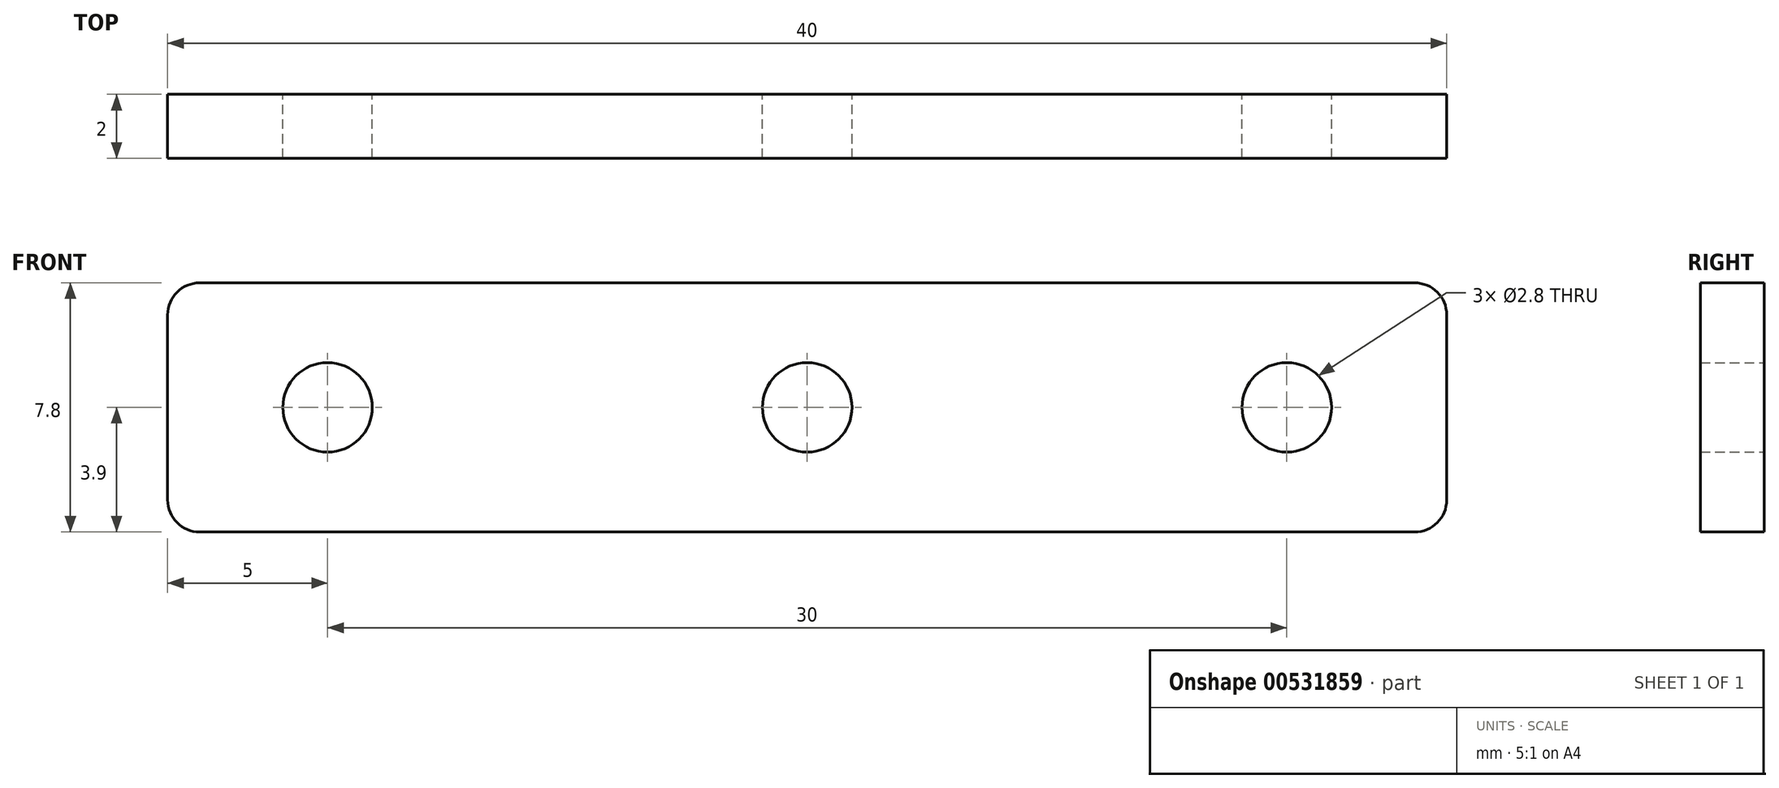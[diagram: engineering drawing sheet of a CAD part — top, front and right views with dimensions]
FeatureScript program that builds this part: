
annotation { "Feature Type Name" : "Feature", "Feature Type Description" : "" }
export const myFeature = defineFeature(function(context is Context, id is Id, definition is map)
    precondition{}
    {
        {
            var Q0;
            Q0=qCreatedBy(makeId("Front.planeOp"),FACE);
            var sketch = newSketch(context, id + "F0", { "sketchPlane" : qUnion([Q0])});
            skLineSegment(sketch, "E0.bottom", {"start": v(0, 0) * mm, "end": v(40, 0) * mm});
            skLineSegment(sketch, "E0.top", {"start": v(0, 7.8) * mm, "end": v(40, 7.8) * mm});
            skLineSegment(sketch, "E0.left", {"start": v(0, 0) * mm, "end": v(0, 7.8) * mm});
            skLineSegment(sketch, "E0.right", {"start": v(40, 0) * mm, "end": v(40, 7.8) * mm});
            skLineSegment(sketch, "E1", {"start": v(0, 3.9) * mm, "end": v(10, 3.9) * mm});
            skCircle(sketch, "E2", {"center": v(5, 3.9) * mm, "radius": 1.4 * mm});
            skLineSegment(sketch, "E3", {"start": v(40, 3.9) * mm, "end": v(30, 3.9) * mm});
            skPoint(sketch, "E3.endSnap0", {"position": v(40, 3.9) * mm});
            skCircle(sketch, "E4", {"center": v(35, 3.9) * mm, "radius": 1.4 * mm});
            skLineSegment(sketch, "E5", {"start": v(20, 7.8) * mm, "end": v(20, 3.9) * mm});
            skCircle(sketch, "E6", {"center": v(20, 3.9) * mm, "radius": 1.4 * mm});
            skSolve(sketch);
        }
        {
            var Q0;
            Q0=qSketchRegion(id+"F0",true);
            extrude(context, id + "F1", {"entities" : qUnion([Q0]), "depth" : 2 * mm});
        }
        {
            var Q0;
            Q0=makeQuery(id+"F1.opExtrude","SWEPT_EDGE",EDGE,{"disambiguationData":[OSD([sQuery(id+"F0.wireOp",EDGE,"E0.top"),sQuery(id+"F0.wireOp",EDGE,"E0.left")])]});
            var Q1;
            Q1=makeQuery(id+"F1.opExtrude","SWEPT_EDGE",EDGE,{"disambiguationData":[OSD([sQuery(id+"F0.wireOp",EDGE,"E0.bottom"),sQuery(id+"F0.wireOp",EDGE,"E0.left")])]});
            var Q2;
            Q2=makeQuery(id+"F1.opExtrude","SWEPT_EDGE",EDGE,{"disambiguationData":[OSD([sQuery(id+"F0.wireOp",EDGE,"E0.top"),sQuery(id+"F0.wireOp",EDGE,"E0.right")])]});
            var Q3;
            Q3=makeQuery(id+"F1.opExtrude","SWEPT_EDGE",EDGE,{"disambiguationData":[OSD([sQuery(id+"F0.wireOp",EDGE,"E0.bottom"),sQuery(id+"F0.wireOp",EDGE,"E0.right")])]});
            fillet(context, id + "F2", {"entities" : qUnion([Q0, Q1, Q2, Q3]), "radius" : 1 * mm, "tangentPropagation" : true, "allowEdgeOverflow" : false});
        }
    });
